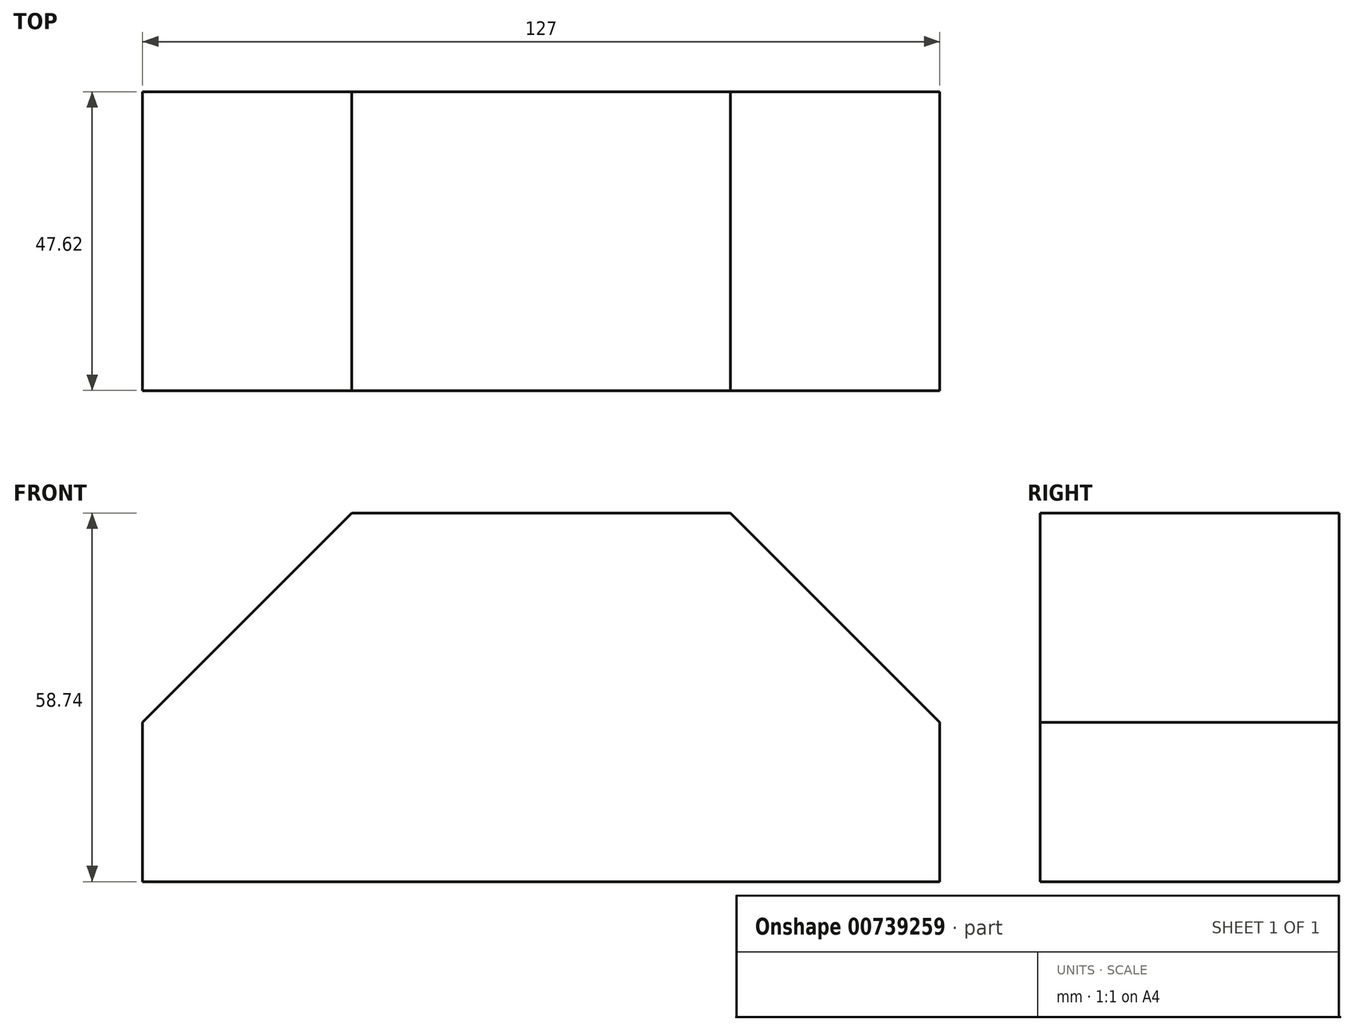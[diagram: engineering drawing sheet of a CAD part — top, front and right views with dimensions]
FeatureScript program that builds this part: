
annotation { "Feature Type Name" : "Feature", "Feature Type Description" : "" }
export const myFeature = defineFeature(function(context is Context, id is Id, definition is map)
    precondition{}
    {
        {
            var Q0;
            Q0=qCreatedBy(makeId("Front.planeOp"),FACE);
            var sketch = newSketch(context, id + "F0", { "sketchPlane" : qUnion([Q0])});
            skLineSegment(sketch, "E0.bottom", {"start": v(0, 0) * mm, "end": v(127, 0) * mm});
            skLineSegment(sketch, "E0.top", {"start": v(0, 58.74) * mm, "end": v(127, 58.74) * mm});
            skLineSegment(sketch, "E0.left", {"start": v(0, 0) * mm, "end": v(0, 58.74) * mm});
            skLineSegment(sketch, "E0.right", {"start": v(127, 0) * mm, "end": v(127, 58.74) * mm});
            skLineSegment(sketch, "E1", {"start": v(0, 58.74) * mm, "end": v(33.34, 58.74) * mm});
            skLineSegment(sketch, "E2", {"start": v(0, 58.74) * mm, "end": v(0, 25.4) * mm});
            skLineSegment(sketch, "E3", {"start": v(0, 25.4) * mm, "end": v(33.34, 58.74) * mm});
            skLineSegment(sketch, "E4", {"start": v(127, 58.74) * mm, "end": v(93.66, 58.74) * mm});
            skLineSegment(sketch, "E5", {"start": v(93.66, 58.74) * mm, "end": v(127, 25.4) * mm});
            skLineSegment(sketch, "E6", {"start": v(127, 25.4) * mm, "end": v(127, 58.74) * mm});
            skSolve(sketch);
        }
        {
            var Q0;
            Q0=makeQuery(id+"F0.imprint","IMPRINT",FACE,{"disambiguationData":[TD([[makeQuery(id+"F0.imprint","IMPRINT",EDGE,{"derivedFrom":sQuery(id+"F0.wireOp",EDGE,"E0.bottom")}),1.0]])]});
            extrude(context, id + "F1", {"entities" : qUnion([Q0]), "depth" : 47.62 * mm, "offsetDistance" : 25.4 * mm});
        }
    });
